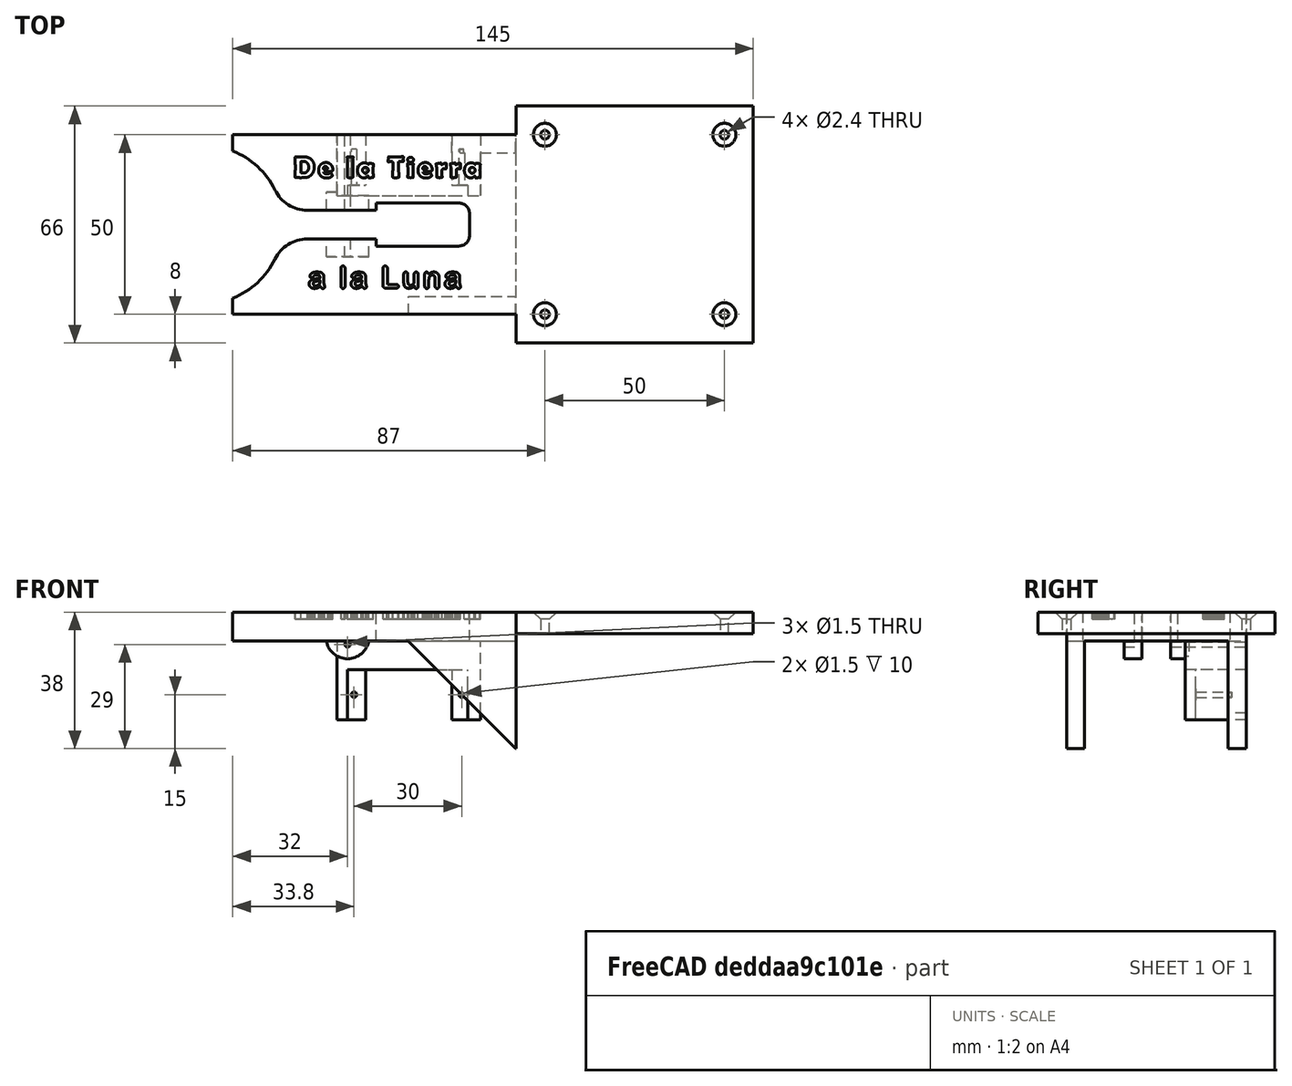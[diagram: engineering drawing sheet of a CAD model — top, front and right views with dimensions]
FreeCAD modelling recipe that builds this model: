
FCSTD DOCUMENT  (FreeCAD 0.20R29603 (Git))
Label: Plataforma_Lanzadera
License: All rights reserved
LicenseURL: http://en.wikipedia.org/wiki/All_rights_reserved
objects: Part::Cut×35, Part::Cylinder×31, Part::Feature×26, Part::Box×19, Part::MultiFuse×17, Part::Fillet×10, Part::Chamfer×4, Part::Extrusion×2
note: 144 computed .brp shape members not serialized (recipe doc carries the construction recipe); baked Part::Feature solids carry a one-line shape summary decoded from their .brp

FEATURE [Part::Box] Box079  label="Cubo079"
  AttacherType = Attacher::AttachEngine3D
  Height = 8
  Length = 145
  Placement = pos=(8,-25,145) rot=(0,0,1;0rad)
  Width = 50
FEATURE [Part::Box] Box080  label="Cubo080"
  AttacherType = Attacher::AttachEngine3D
  Height = 8
  Length = 66
  Placement = pos=(87,-33,139) rot=(0,0,1;0rad)
  Width = 66
FEATURE [Part::Box] Box087  label="Cubo087"
  AttacherType = Attacher::AttachEngine3D
  Height = 6
  Length = 66
  Placement = pos=(87,-33,147) rot=(0,0,1;0rad)
  Width = 66
FEATURE [Part::Box] Box088  label="Cubo088"
  AttacherType = Attacher::AttachEngine3D
  Height = 30
  Length = 30
  Placement = pos=(57,0,115) rot=(0,0,1;0rad)
  Width = 5
FEATURE [Part::Box] Box089  label="Cubo089"
  AttacherType = Attacher::AttachEngine3D
  Height = 60
  Length = 60
  Placement = pos=(13,0,104) rot=(0,1,0;0.785398rad)
  Width = 5
FEATURE [Part::Box] Box090  label="Cubo090"
  AttacherType = Attacher::AttachEngine3D
  Height = 30
  Length = 30
  Placement = pos=(57,0,115) rot=(0,0,1;0rad)
  Width = 5
FEATURE [Part::Box] Box091  label="Cubo091"
  AttacherType = Attacher::AttachEngine3D
  Height = 60
  Length = 60
  Placement = pos=(13,0,104) rot=(0,1,0;0.785398rad)
  Width = 5
FEATURE [Part::Box] Box251  label="Cubo237"
  AttacherType = Attacher::AttachEngine3D
  Height = 13
  Length = 50
  Placement = pos=(21,-4,143) rot=(0,0,1;0rad)
  Width = 8
FEATURE [Part::Box] Box254  label="Cubo240"
  AttacherType = Attacher::AttachEngine3D
  Height = 25
  Length = 40
  Placement = pos=(38,6,128) rot=(0,0,1;0rad)
  Width = 17
FEATURE [Part::Box] Box255  label="Cubo241"
  AttacherType = Attacher::AttachEngine3D
  Height = 23
  Length = 24
  Width = 14
FEATURE [Part::Box] Box256  label="Cubo242"
  AttacherType = Attacher::AttachEngine3D
  Height = 3
  Length = 33.5
  Placement = pos=(-5,0,16) rot=(0,0,1;0rad)
  Width = 14
FEATURE [Part::Box] Box257  label="Cubo243"
  AttacherType = Attacher::AttachEngine3D
  Height = 1.4
  Length = 13
  Placement = pos=(9.8,5,28.6) rot=(0,0,1;0rad)
  Width = 4
FEATURE [Part::Box] Box258  label="Cubo244"
  AttacherType = Attacher::AttachEngine3D
  Height = 6
  Length = 6
  Placement = pos=(41,2,134) rot=(0,0,1;0rad)
  Width = 7
FEATURE [Part::Box] Box259  label="Cubo245"
  AttacherType = Attacher::AttachEngine3D
  Height = 6
  Length = 6
  Placement = pos=(68.5,2,134) rot=(0,0,1;0rad)
  Width = 7
FEATURE [Part::Box] Box260  label="Cubo246"
  AttacherType = Attacher::AttachEngine3D
  Height = 23
  Length = 24
  Width = 14
FEATURE [Part::Box] Box261  label="Cubo247"
  AttacherType = Attacher::AttachEngine3D
  Height = 3
  Length = 33.5
  Placement = pos=(-5,0,16) rot=(0,0,1;0rad)
  Width = 14
FEATURE [Part::Box] Box262  label="Cubo248"
  AttacherType = Attacher::AttachEngine3D
  Height = 1.4
  Length = 13
  Placement = pos=(9.8,5,28.6) rot=(0,0,1;0rad)
  Width = 4
FEATURE [Part::Box] Box263  label="Cubo249"
  AttacherType = Attacher::AttachEngine3D
  Height = 15
  Length = 26
  Placement = pos=(48,-6,140) rot=(0,0,1;0rad)
  Width = 12
FEATURE [Part::Box] Box264  label="Cubo250"
  AttacherType = Attacher::AttachEngine3D
  Height = 10
  Length = 45
  Placement = pos=(33,0,113) rot=(0,0,1;0rad)
  Width = 39
FEATURE [Part::Cut] Cut075
  Base = -> Box088
  Placement = pos=(0,20,0) rot=(0,0,1;0rad)
  Tool = -> Box089
FEATURE [Part::Cut] Cut076
  Base = -> Box090
  Placement = pos=(0,-25,0) rot=(0,0,1;0rad)
  Tool = -> Box091
FEATURE [Part::Cylinder] Cylinder048  label="Cilindro048"
  Angle = 360
  AttacherType = Attacher::AttachEngine3D
  FirstAngle = 0
  Height = 200
  Radius = 22
  SecondAngle = 0
FEATURE [Part::Cut] Cut067
  Base = -> Box079
  Tool = -> Cylinder048
FEATURE [Part::Cylinder] Cylinder053  label="Cilindro053"
  Angle = 360
  AttacherType = Attacher::AttachEngine3D
  FirstAngle = 0
  Height = 40
  Placement = pos=(95,-25,130) rot=(0,0,1;0rad)
  Radius = 1.2
  SecondAngle = 0
FEATURE [Part::Cylinder] Cylinder054  label="Cilindro054"
  Angle = 360
  AttacherType = Attacher::AttachEngine3D
  FirstAngle = 0
  Height = 40
  Placement = pos=(145,25,130) rot=(0,0,1;0rad)
  Radius = 1.2
  SecondAngle = 0
FEATURE [Part::Cylinder] Cylinder055  label="Cilindro055"
  Angle = 360
  AttacherType = Attacher::AttachEngine3D
  FirstAngle = 0
  Height = 40
  Placement = pos=(95,25,130) rot=(0,0,1;0rad)
  Radius = 1.2
  SecondAngle = 0
FEATURE [Part::Cylinder] Cylinder056  label="Cilindro056"
  Angle = 360
  AttacherType = Attacher::AttachEngine3D
  FirstAngle = 0
  Height = 40
  Placement = pos=(145,-25,130) rot=(0,0,1;0rad)
  Radius = 1.2
  SecondAngle = 0
FEATURE [Part::Cylinder] Cylinder212  label="Cilindro212"
  Angle = 360
  AttacherType = Attacher::AttachEngine3D
  FirstAngle = 0
  Height = 5
  Placement = pos=(40,9,146) rot=(1,0,0;1.5708rad)
  Radius = 6
  SecondAngle = 0
FEATURE [Part::Cylinder] Cylinder215  label="Cilindro215"
  Angle = 360
  AttacherType = Attacher::AttachEngine3D
  FirstAngle = 0
  Height = 5
  Placement = pos=(40,-4,146) rot=(1,0,0;1.5708rad)
  Radius = 6
  SecondAngle = 0
FEATURE [Part::Cylinder] Cylinder216  label="Cilindro216"
  Angle = 360
  AttacherType = Attacher::AttachEngine3D
  FirstAngle = 0
  Height = 60
  Placement = pos=(40,23,144) rot=(1,0,0;1.5708rad)
  Radius = 0.75
  SecondAngle = 0
FEATURE [Part::Cylinder] Cylinder218  label="Cilindro218"
  Angle = 360
  AttacherType = Attacher::AttachEngine3D
  FirstAngle = 0
  Height = 3
  Placement = pos=(7,7,23) rot=(0,0,1;0rad)
  Radius = 7
  SecondAngle = 0
FEATURE [Part::Cylinder] Cylinder219  label="Cilindro219"
  Angle = 360
  AttacherType = Attacher::AttachEngine3D
  FirstAngle = 0
  Height = 3
  Placement = pos=(14,7,23) rot=(0,0,1;0rad)
  Radius = 2
  SecondAngle = 0
FEATURE [Part::Cylinder] Cylinder220  label="Cilindro220"
  Angle = 360
  AttacherType = Attacher::AttachEngine3D
  FirstAngle = 0
  Height = 10
  Placement = pos=(-3.2,7,12) rot=(0,0,1;0rad)
  Radius = 1.65
  SecondAngle = 0
FEATURE [Part::Cylinder] Cylinder221  label="Cilindro221"
  Angle = 360
  AttacherType = Attacher::AttachEngine3D
  FirstAngle = 0
  Height = 10
  Placement = pos=(26.8,7,12) rot=(0,0,1;0rad)
  Radius = 1.65
  SecondAngle = 0
FEATURE [Part::Cylinder] Cylinder222  label="Cilindro222"
  Angle = 360
  AttacherType = Attacher::AttachEngine3D
  FirstAngle = 0
  Height = 4
  Placement = pos=(7,7,26) rot=(0,0,1;0rad)
  Radius = 3.5
  SecondAngle = 0
FEATURE [Part::Cylinder] Cylinder223  label="Cilindro223"
  Angle = 360
  AttacherType = Attacher::AttachEngine3D
  FirstAngle = 0
  Height = 10
  Placement = pos=(21,7,25) rot=(0,0,1;0rad)
  Radius = 0.25
  SecondAngle = 0
FEATURE [Part::Cylinder] Cylinder224  label="Cilindro224"
  Angle = 360
  AttacherType = Attacher::AttachEngine3D
  FirstAngle = 0
  Height = 10
  Placement = pos=(19,7,25) rot=(0,0,1;0rad)
  Radius = 0.25
  SecondAngle = 0
FEATURE [Part::Cylinder] Cylinder225  label="Cilindro225"
  Angle = 360
  AttacherType = Attacher::AttachEngine3D
  FirstAngle = 0
  Height = 10
  Placement = pos=(17,7,25) rot=(0,0,1;0rad)
  Radius = 0.25
  SecondAngle = 0
FEATURE [Part::Cylinder] Cylinder226  label="Cilindro226"
  Angle = 360
  AttacherType = Attacher::AttachEngine3D
  FirstAngle = 0
  Height = 10
  Placement = pos=(15,7,27) rot=(0,0,1;0rad)
  Radius = 0.25
  SecondAngle = 0
FEATURE [Part::Cylinder] Cylinder227  label="Cilindro227"
  Angle = 360
  AttacherType = Attacher::AttachEngine3D
  FirstAngle = 0
  Height = 10
  Placement = pos=(13,7,27) rot=(0,0,1;0rad)
  Radius = 0.25
  SecondAngle = 0
FEATURE [Part::Cylinder] Cylinder228  label="Cilindro228"
  Angle = 360
  AttacherType = Attacher::AttachEngine3D
  FirstAngle = 0
  Height = 10
  Placement = pos=(42.8,19,138) rot=(1,0,0;1.5708rad)
  Radius = 0.75
  SecondAngle = 0
FEATURE [Part::Cylinder] Cylinder229  label="Cilindro229"
  Angle = 360
  AttacherType = Attacher::AttachEngine3D
  FirstAngle = 0
  Height = 10
  Placement = pos=(72.8,19,138) rot=(1,0,0;1.5708rad)
  Radius = 0.75
  SecondAngle = 0
FEATURE [Part::Cylinder] Cylinder230  label="Cilindro230"
  Angle = 360
  AttacherType = Attacher::AttachEngine3D
  FirstAngle = 0
  Height = 3
  Placement = pos=(7,7,23) rot=(0,0,1;0rad)
  Radius = 7
  SecondAngle = 0
FEATURE [Part::Cylinder] Cylinder231  label="Cilindro231"
  Angle = 360
  AttacherType = Attacher::AttachEngine3D
  FirstAngle = 0
  Height = 3
  Placement = pos=(14,7,23) rot=(0,0,1;0rad)
  Radius = 2
  SecondAngle = 0
FEATURE [Part::Cylinder] Cylinder232  label="Cilindro232"
  Angle = 360
  AttacherType = Attacher::AttachEngine3D
  FirstAngle = 0
  Height = 10
  Placement = pos=(-3.2,7,12) rot=(0,0,1;0rad)
  Radius = 1.65
  SecondAngle = 0
FEATURE [Part::Cylinder] Cylinder233  label="Cilindro233"
  Angle = 360
  AttacherType = Attacher::AttachEngine3D
  FirstAngle = 0
  Height = 10
  Placement = pos=(26.8,7,12) rot=(0,0,1;0rad)
  Radius = 1.65
  SecondAngle = 0
FEATURE [Part::Cylinder] Cylinder234  label="Cilindro234"
  Angle = 360
  AttacherType = Attacher::AttachEngine3D
  FirstAngle = 0
  Height = 4
  Placement = pos=(7,7,26) rot=(0,0,1;0rad)
  Radius = 3.5
  SecondAngle = 0
FEATURE [Part::Cylinder] Cylinder235  label="Cilindro235"
  Angle = 360
  AttacherType = Attacher::AttachEngine3D
  FirstAngle = 0
  Height = 10
  Placement = pos=(21,7,25) rot=(0,0,1;0rad)
  Radius = 0.25
  SecondAngle = 0
FEATURE [Part::Cylinder] Cylinder236  label="Cilindro236"
  Angle = 360
  AttacherType = Attacher::AttachEngine3D
  FirstAngle = 0
  Height = 10
  Placement = pos=(19,7,25) rot=(0,0,1;0rad)
  Radius = 0.25
  SecondAngle = 0
FEATURE [Part::Cylinder] Cylinder237  label="Cilindro237"
  Angle = 360
  AttacherType = Attacher::AttachEngine3D
  FirstAngle = 0
  Height = 10
  Placement = pos=(17,7,25) rot=(0,0,1;0rad)
  Radius = 0.25
  SecondAngle = 0
FEATURE [Part::Cylinder] Cylinder238  label="Cilindro238"
  Angle = 360
  AttacherType = Attacher::AttachEngine3D
  FirstAngle = 0
  Height = 10
  Placement = pos=(15,7,27) rot=(0,0,1;0rad)
  Radius = 0.25
  SecondAngle = 0
FEATURE [Part::Cylinder] Cylinder239  label="Cilindro239"
  Angle = 360
  AttacherType = Attacher::AttachEngine3D
  FirstAngle = 0
  Height = 10
  Placement = pos=(13,7,27) rot=(0,0,1;0rad)
  Radius = 0.25
  SecondAngle = 0
FEATURE [Part::Cylinder] Cylinder240  label="Cilindro240"
  Angle = 360
  AttacherType = Attacher::AttachEngine3D
  FirstAngle = 0
  Height = 60
  Placement = pos=(40,36,144) rot=(1,0,0;1.5708rad)
  Radius = 0.75
  SecondAngle = 0
FEATURE [Part::MultiFuse] Fusion061
  Shapes = -> [Cut067,Box087]
FEATURE [Part::Cut] Cut074  label="Plataforma"
  Base = -> Fusion061
  Tool = -> Box080
FEATURE [Part::MultiFuse] Fusion062
  Shapes = -> [Cut074,Cut075,Cut076]
FEATURE [Part::Cut] Cut077
  Base = -> Fusion062
  Tool = -> Cylinder053
FEATURE [Part::Cut] Cut078
  Base = -> Cut077
  Tool = -> Cylinder054
FEATURE [Part::Cut] Cut079
  Base = -> Cut078
  Tool = -> Cylinder055
FEATURE [Part::Cut] Cut080
  Base = -> Cut079
  Tool = -> Cylinder056
FEATURE [Part::Chamfer] Chamfer029
  Base = -> Cut080
  Edges = 2 edges r=2: [Edge8,Edge32]
FEATURE [Part::Chamfer] Chamfer030
  Base = -> Chamfer029
  Edges = 2 edges r=2: [Edge2,Edge16]
FEATURE [Part::Chamfer] Chamfer031
  Base = -> Chamfer030
  Edges = 2 edges r=2: [Edge15,Edge42]
FEATURE [Part::Chamfer] Chamfer032  label="Plataforma001"
  Base = -> Chamfer031
  Edges = 2 edges r=2: [Edge12,Edge13]
FEATURE [Part::Cut] Cut286
  Base = -> Chamfer032
  Tool = -> Box251
FEATURE [Part::Fillet] Fillet191
  Base = -> Cut286
  Edges = 1 edges r=10: [Edge67]
FEATURE [Part::Fillet] Fillet192
  Base = -> Fillet191
  Edges = 1 edges r=10: [Edge21]
FEATURE [Part::MultiFuse] Fusion162
  Shapes = -> [Cylinder212,Fillet192]
FEATURE [Part::MultiFuse] Fusion163
  Shapes = -> [Cylinder215,Fusion162]
FEATURE [Part::Cut] Cut289
  Base = -> Fusion163
  Tool = -> Cylinder216
FEATURE [Part::MultiFuse] Fusion164
  Shapes = -> [Cylinder218,Cylinder219]
FEATURE [Part::MultiFuse] Fusion165
  Shapes = -> [Box255,Fusion164]
FEATURE [Part::MultiFuse] Fusion166
  Shapes = -> [Fusion165,Box256]
FEATURE [Part::Cut] Cut291
  Base = -> Fusion166
  Tool = -> Cylinder220
FEATURE [Part::Cut] Cut292  label="Servo009"
  Base = -> Cut291
  Tool = -> Cylinder221
FEATURE [Part::MultiFuse] Fusion167
  Shapes = -> [Cylinder222,Box257]
FEATURE [Part::Fillet] Fillet198
  Base = -> Fusion167
  Edges = 1 edges r=2: [Edge4]
FEATURE [Part::Fillet] Fillet199
  Base = -> Fillet198
  Edges = 1 edges r=1: [Edge25]
FEATURE [Part::Fillet] Fillet200
  Base = -> Fillet199
  Edges = 1 edges r=1: [Edge17]
FEATURE [Part::MultiFuse] Fusion168
  Shapes = -> [Cut292,Fillet200]
FEATURE [Part::Cut] Cut293
  Base = -> Fusion168
  Tool = -> Cylinder223
FEATURE [Part::Cut] Cut294
  Base = -> Cut293
  Tool = -> Cylinder227
FEATURE [Part::Cut] Cut295
  Base = -> Cut294
  Tool = -> Cylinder226
FEATURE [Part::Cut] Cut296
  Base = -> Cut295
  Tool = -> Cylinder225
FEATURE [Part::Cut] Cut297  label="Servo010"
  Base = -> Cut296
  Placement = pos=(46,25,131) rot=(1,0,0;1.5708rad)
  Tool = -> Cylinder224
FEATURE [Part::Cut] Cut298
  Base = -> Box254
  Tool = -> Cut297
FEATURE [Part::Cut] Cut299
  Base = -> Cut298
  Tool = -> Box258
FEATURE [Part::Cut] Cut300
  Base = -> Cut299
  Tool = -> Box259
FEATURE [Part::Cut] Cut301
  Base = -> Cut300
  Tool = -> Cylinder228
FEATURE [Part::Cut] Cut302
  Base = -> Cut301
  Placement = pos=(-1,2,-8) rot=(1,0,0;0rad)
  Tool = -> Cylinder229
FEATURE [Part::MultiFuse] Fusion169
  Shapes = -> [Cylinder230,Cylinder231]
FEATURE [Part::MultiFuse] Fusion170
  Shapes = -> [Box260,Fusion169]
FEATURE [Part::MultiFuse] Fusion171
  Shapes = -> [Fusion170,Box261]
FEATURE [Part::Cut] Cut303
  Base = -> Fusion171
  Tool = -> Cylinder232
FEATURE [Part::Cut] Cut304  label="Servo011"
  Base = -> Cut303
  Tool = -> Cylinder233
FEATURE [Part::MultiFuse] Fusion172
  Shapes = -> [Cylinder234,Box262]
FEATURE [Part::Fillet] Fillet201
  Base = -> Fusion172
  Edges = 1 edges r=2: [Edge4]
FEATURE [Part::Fillet] Fillet202
  Base = -> Fillet201
  Edges = 1 edges r=1: [Edge25]
FEATURE [Part::Fillet] Fillet203
  Base = -> Fillet202
  Edges = 1 edges r=1: [Edge17]
FEATURE [Part::MultiFuse] Fusion173
  Shapes = -> [Cut304,Fillet203]
FEATURE [Part::Cut] Cut305
  Base = -> Fusion173
  Tool = -> Cylinder235
FEATURE [Part::Cut] Cut306
  Base = -> Cut305
  Tool = -> Cylinder239
FEATURE [Part::Cut] Cut307
  Base = -> Cut306
  Tool = -> Cylinder238
FEATURE [Part::Cut] Cut308
  Base = -> Cut307
  Tool = -> Cylinder237
FEATURE [Part::Cut] Cut309  label="Servo012"
  Base = -> Cut308
  Placement = pos=(45,27,123) rot=(1,0,0;1.5708rad)
  Tool = -> Cylinder236
FEATURE [Part::Cut] Cut310
  Base = -> Cut289
  Tool = -> Cut309
FEATURE [Part::MultiFuse] Fusion174
  Shapes = -> [Cut302,Cut310]
FEATURE [Part::Cut] Cut312
  Base = -> Fusion174
  Tool = -> Cylinder240
FEATURE [Part::Cut] Cut313
  Base = -> Cut312
  Tool = -> Box263
FEATURE [Part::Fillet] Fillet204
  Base = -> Cut313
  Edges = 1 edges r=3: [Edge139]
FEATURE [Part::Fillet] Fillet205  label="Plataforma002"
  Base = -> Fillet204
  Edges = 1 edges r=3: [Edge25]
FEATURE [Part::Cut] Cut317
  Base = -> Fillet205
  Tool = -> Box264
FEATURE [Part::Feature] path178783
  shape: bbox 5.378 x 5.833 x 3.003e-07 mm, 0 faces, 0 solids (baked)
FEATURE [Part::Feature] path178783001
  shape: bbox 2.187 x 3.262 x 3.003e-07 mm, 0 faces, 0 solids (baked)
FEATURE [Part::Feature] path178785
  shape: bbox 3.969 x 4.32 x 3.003e-07 mm, 0 faces, 0 solids (baked)
FEATURE [Part::Feature] path178785001
  shape: bbox 1.203 x 0.8062 x 3.003e-07 mm, 0 faces, 0 solids (baked)
FEATURE [Part::Feature] path178787
  shape: bbox 1.687 x 5.842 x 3.003e-07 mm, 0 faces, 0 solids (baked)
FEATURE [Part::Feature] path178789
  shape: bbox 4.473 x 4.2 x 3.003e-07 mm, 0 faces, 0 solids (baked)
FEATURE [Part::Feature] path178789001
  shape: bbox 1.592 x 1.625 x 3.003e-07 mm, 0 faces, 0 solids (baked)
FEATURE [Part::Feature] path178791
  shape: bbox 4.362 x 5.883 x 3.003e-07 mm, 0 faces, 0 solids (baked)
FEATURE [Part::Feature] path178793
  shape: bbox 1.633 x 1.439 x 3.003e-07 mm, 0 faces, 0 solids (baked)
FEATURE [Part::Feature] path178793001
  shape: bbox 1.641 x 3.96 x 3.003e-07 mm, 0 faces, 0 solids (baked)
FEATURE [Part::Feature] path178795
  shape: bbox 3.969 x 4.32 x 3.003e-07 mm, 0 faces, 0 solids (baked)
FEATURE [Part::Feature] path178795001
  shape: bbox 1.203 x 0.8062 x 3.003e-07 mm, 0 faces, 0 solids (baked)
FEATURE [Part::Feature] path178797
  shape: bbox 2.906 x 4.105 x 3.003e-07 mm, 0 faces, 0 solids (baked)
FEATURE [Part::Feature] path178799
  shape: bbox 2.906 x 4.105 x 3.003e-07 mm, 0 faces, 0 solids (baked)
FEATURE [Part::Feature] path178801
  shape: bbox 4.473 x 4.2 x 3.003e-07 mm, 0 faces, 0 solids (baked)
FEATURE [Part::Feature] path178801001
  shape: bbox 1.592 x 1.625 x 3.003e-07 mm, 0 faces, 0 solids (baked)
FEATURE [Part::MultiFuse] Fusion175
  Shapes = -> [path178783,path178783001,path178785,path178785001,path178787,path178789,path178789001,path178791,path178793,path178793001,path178795,path178795001,path178797,path178799,path178801,path178801001]
FEATURE [Part::Extrusion] Extrude
  Base = -> Fusion175
  Dir = (0,0,1)
  DirMode = 2
  FaceMakerClass = Part::FaceMakerBullseye
  LengthFwd = 5
  LengthRev = 0
  Placement = pos=(45,16,151) rot=(0,0,1;0rad)
  Solid = true
  Symmetric = false
FEATURE [Part::Cut] Cut318
  Base = -> Cut317
  Tool = -> Extrude
FEATURE [Part::Feature] path240932
  shape: bbox 4.333 x 4.597 x 3.003e-07 mm, 0 faces, 0 solids (baked)
FEATURE [Part::Feature] path240932001
  shape: bbox 1.889 x 1.53 x 3.003e-07 mm, 0 faces, 0 solids (baked)
FEATURE [Part::Feature] path240934
  shape: bbox 1.129 x 6.267 x 3.003e-07 mm, 0 faces, 0 solids (baked)
FEATURE [Part::Feature] path240936
  shape: bbox 4.333 x 4.597 x 3.003e-07 mm, 0 faces, 0 solids (baked)
FEATURE [Part::Feature] path240936001
  shape: bbox 1.889 x 1.53 x 3.003e-07 mm, 0 faces, 0 solids (baked)
FEATURE [Part::Feature] path240938
  shape: bbox 4.333 x 6.164 x 3.003e-07 mm, 0 faces, 0 solids (baked)
FEATURE [Part::Feature] path240940
  shape: bbox 4.022 x 4.589 x 3.003e-07 mm, 0 faces, 0 solids (baked)
FEATURE [Part::Feature] path240942
  shape: bbox 4.023 x 4.589 x 3.003e-07 mm, 0 faces, 0 solids (baked)
FEATURE [Part::Feature] path240944
  shape: bbox 4.333 x 4.597 x 3.003e-07 mm, 0 faces, 0 solids (baked)
FEATURE [Part::Feature] path240944001
  shape: bbox 1.889 x 1.53 x 3.003e-07 mm, 0 faces, 0 solids (baked)
FEATURE [Part::MultiFuse] Fusion176
  Shapes = -> [path240932,path240932001,path240934,path240936,path240936001,path240938,path240940,path240942,path240944,path240944001]
FEATURE [Part::Extrusion] Extrude001
  Base = -> Fusion176
  Dir = (0,0,1)
  DirMode = 2
  FaceMakerClass = Part::FaceMakerBullseye
  LengthFwd = 5
  LengthRev = 0
  Placement = pos=(48,-15,151) rot=(0,0,1;0rad)
  Solid = true
  Symmetric = false
FEATURE [Part::Cut] Cut319  label="Lanzadera"
  Base = -> Cut318
  Placement = pos=(-90,0,-135) rot=(0,0,1;0rad)
  Tool = -> Extrude001
